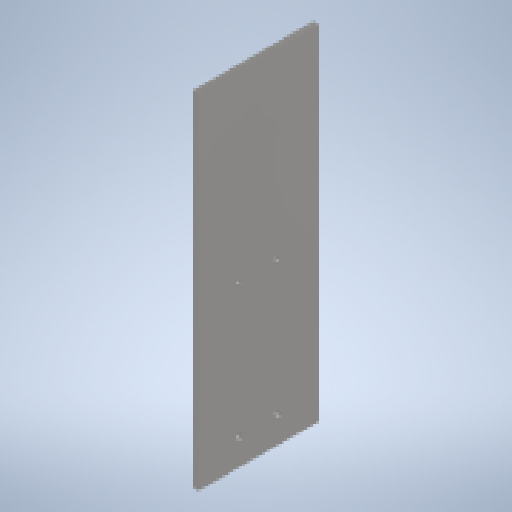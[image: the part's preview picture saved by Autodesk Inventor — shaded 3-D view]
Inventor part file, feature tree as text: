
AUTODESK INVENTOR PART (.ipt)
format: ipt  version: 2025.2 (Build 292293000, 293)  size: 154,112 bytes
history: native  units: in
note: dims shown in document units (in); Inventor stores cm internally (conversion verified against a paired STEP export)
features: extrude x4, other x4, reference x2, projected_geometry x1
ambient origin geometry x8: Origin, YZ Plane, XZ Plane, XY Plane, X Axis, Y Axis, Z Axis, Center Point
bodies: Solid1 (feature_tree)
feature tree (11):
  extrude  "Extrusion1"  Depth=8.3622in
  extrude  "Extrusion2"  Depth=5.5906in
  extrude  "Extrusion3"  Depth=0.258in TaperAngle=0.0deg
  extrude  "Extrusion4"  Depth=0.3in TaperAngle=0.0deg
  projected_geometry  "Projected Loop1"
  reference  "Reference1"
  reference  "Reference2"
  parser-record x1  (decoder bookkeeping rows leaked as tree rows — omitted from the tree; the rows remain in map.json)
  other  "Z_GANTRY.iam"
  other  "Ballscrew_Assembly_1204:1"
  other  "2x3_Tube_Short:1"
note: 1 file-system path scrubbed to <path> (originals preserved in map.json)
